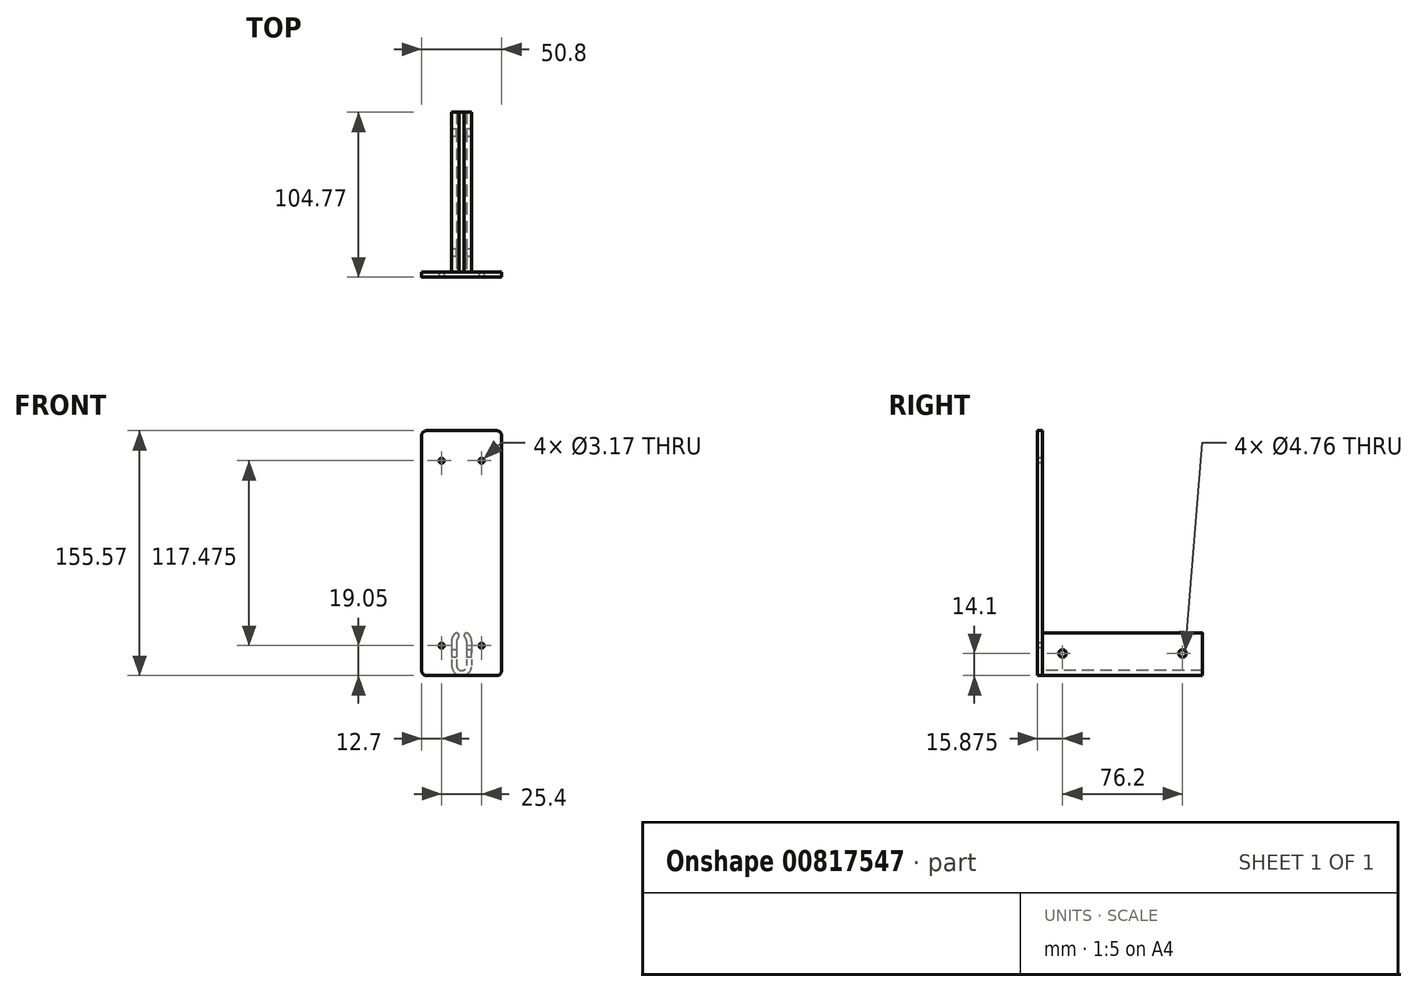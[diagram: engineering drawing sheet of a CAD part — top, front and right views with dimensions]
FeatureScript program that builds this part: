
annotation { "Feature Type Name" : "Feature", "Feature Type Description" : "" }
export const myFeature = defineFeature(function(context is Context, id is Id, definition is map)
    precondition{}
    {
        {
            var Q0;
            Q0=qCreatedBy(makeId("Front.planeOp"),FACE);
            var sketch = newSketch(context, id + "F0", { "sketchPlane" : qUnion([Q0])});
            skLineSegment(sketch, "E0.bottom", {"start": v(-3.18, 0) * mm, "end": v(-47.63, 0) * mm});
            skLineSegment(sketch, "E0.top", {"start": v(-3.18, 155.58) * mm, "end": v(-47.63, 155.58) * mm});
            skLineSegment(sketch, "E0.left", {"start": v(0, 3.17) * mm, "end": v(0, 152.4) * mm});
            skLineSegment(sketch, "E0.right", {"start": v(-50.8, 3.17) * mm, "end": v(-50.8, 152.4) * mm});
            skCircle(sketch, "E1", {"center": v(-38.1, 136.53) * mm, "radius": 1.59 * mm});
            skCircle(sketch, "E2", {"center": v(-12.7, 136.53) * mm, "radius": 1.59 * mm});
            skCircle(sketch, "E3", {"center": v(-12.7, 19.05) * mm, "radius": 1.59 * mm});
            skCircle(sketch, "E4", {"center": v(-38.1, 19.05) * mm, "radius": 1.59 * mm});
            skPoint(sketch, "E5.visualSharp", {"position": v(-50.8, 155.58) * mm});
            skArc(sketch, "E5.filletArc", {"start": v(-47.63, 155.58) * mm, "mid": v(-49.87, 154.65) * mm, "end": v(-50.8, 152.4) * mm});
            skPoint(sketch, "E6.visualSharp", {"position": v(0, 155.58) * mm});
            skArc(sketch, "E6.filletArc", {"start": v(0, 152.4) * mm, "mid": v(-0.93, 154.65) * mm, "end": v(-3.18, 155.58) * mm});
            skPoint(sketch, "E7.visualSharp", {"position": v(0, 0) * mm});
            skArc(sketch, "E7.filletArc", {"start": v(-3.18, 0) * mm, "mid": v(-0.93, 0.93) * mm, "end": v(0, 3.17) * mm});
            skPoint(sketch, "E8.visualSharp", {"position": v(-50.8, 0) * mm});
            skArc(sketch, "E8.filletArc", {"start": v(-50.8, 3.17) * mm, "mid": v(-49.87, 0.93) * mm, "end": v(-47.63, 0) * mm});
            skSolve(sketch);
        }
        {
            var Q0;
            Q0 = qSketchRegion(id + "F0", true);
            extrude(context, id + "F1", {"entities" : qUnion([Q0]), "oppositeDirection" : true, "depth" : 3.17 * mm, "offsetDistance" : 25.4 * mm});
        }
        {
            var Q0;
            Q0=makeQuery(id+"F1.opExtrude","CAP_FACE",FACE,{"disambiguationData":[OSD([sQuery(id+"F0.wireOp",EDGE,"E0.bottom"),sQuery(id+"F0.wireOp",EDGE,"E0.top"),sQuery(id+"F0.wireOp",EDGE,"E0.left"),sQuery(id+"F0.wireOp",EDGE,"E0.right"),sQuery(id+"F0.wireOp",EDGE,"E1"),sQuery(id+"F0.wireOp",EDGE,"E2"),sQuery(id+"F0.wireOp",EDGE,"E3"),sQuery(id+"F0.wireOp",EDGE,"E4"),sQuery(id+"F0.wireOp",EDGE,"E5.filletArc"),sQuery(id+"F0.wireOp",EDGE,"E6.filletArc"),sQuery(id+"F0.wireOp",EDGE,"E7.filletArc"),sQuery(id+"F0.wireOp",EDGE,"E8.filletArc")])],"isStart":false});
            var sketch = newSketch(context, id + "F2", { "sketchPlane" : qUnion([Q0])});
            skLineSegment(sketch, "E9", {"start": v(25.4, 21.85) * mm, "end": v(25.4, 21.85) * mm, "construction": true});
            skLineSegment(sketch, "E10.0", {"start": v(28.58, 21.85) * mm, "end": v(28.58, 6.35) * mm});
            skLineSegment(sketch, "E11.0", {"start": v(22.23, 21.85) * mm, "end": v(22.23, 6.35) * mm});
            skArc(sketch, "E12", {"start": v(22.23, 6.35) * mm, "mid": v(25.4, 3.18) * mm, "end": v(28.58, 6.35) * mm});
            skPoint(sketch, "E13.orphan", {"position": v(25.4, 155.58) * mm});
            skArc(sketch, "E14", {"start": v(26.99, 25.4) * mm, "mid": v(27.13, 24.75) * mm, "end": v(27.52, 24.22) * mm});
            skArc(sketch, "E15", {"start": v(23.28, 24.22) * mm, "mid": v(23.67, 24.75) * mm, "end": v(23.81, 25.4) * mm});
            skPoint(sketch, "E16.visualSharp", {"position": v(28.58, 23.81) * mm});
            skArc(sketch, "E16.filletArc", {"start": v(28.58, 21.85) * mm, "mid": v(28.3, 23.15) * mm, "end": v(27.52, 24.22) * mm});
            skPoint(sketch, "E17.visualSharp", {"position": v(22.23, 23.81) * mm});
            skArc(sketch, "E17.filletArc", {"start": v(23.28, 24.22) * mm, "mid": v(22.5, 23.15) * mm, "end": v(22.23, 21.85) * mm});
            skPoint(sketch, "E18.trimOffspring.end.orphan", {"position": v(25.4, 0) * mm});
            skArc(sketch, "E19.0", {"start": v(31.75, 21.85) * mm, "mid": v(31.2, 24.44) * mm, "end": v(29.63, 26.58) * mm});
            skArc(sketch, "E19.1", {"start": v(21.17, 26.58) * mm, "mid": v(19.6, 24.44) * mm, "end": v(19.05, 21.85) * mm});
            skLineSegment(sketch, "E19.2", {"start": v(19.05, 21.85) * mm, "end": v(19.05, 6.35) * mm});
            skArc(sketch, "E19.3", {"start": v(19.05, 6.35) * mm, "mid": v(25.4, 0) * mm, "end": v(31.75, 6.35) * mm});
            skLineSegment(sketch, "E19.4", {"start": v(31.75, 21.85) * mm, "end": v(31.75, 6.35) * mm});
            skArc(sketch, "E20", {"start": v(29.63, 26.58) * mm, "mid": v(27.93, 26.85) * mm, "end": v(26.99, 25.4) * mm});
            skArc(sketch, "E21", {"start": v(23.81, 25.4) * mm, "mid": v(22.87, 26.85) * mm, "end": v(21.17, 26.58) * mm});
            skSolve(sketch);
        }
        {
            var Q0;
            Q0 = qSketchRegion(id + "F2", true);
            extrude(context, id + "F3", {"entities" : qUnion([Q0]), "operationType" : NewBodyOperationType.ADD, "depth" : 101.6 * mm, "offsetDistance" : 25.4 * mm});
        }
        {
            var Q0;
            Q0=makeQuery(id+"F3.opExtrude","SWEPT_FACE",FACE,{"disambiguationData":[OSD([sQuery(id+"F2.wireOp",EDGE,"E19.2")])]});
            var sketch = newSketch(context, id + "F4", { "sketchPlane" : qUnion([Q0])});
            skLineSegment(sketch, "E22", {"start": v(15.88, 21.85) * mm, "end": v(15.88, 6.35) * mm, "construction": true});
            skLineSegment(sketch, "E23", {"start": v(92.08, 21.85) * mm, "end": v(92.08, 6.35) * mm, "construction": true});
            skCircle(sketch, "E24", {"center": v(15.88, 14.1) * mm, "radius": 2.38 * mm});
            skCircle(sketch, "E25", {"center": v(92.08, 14.1) * mm, "radius": 2.38 * mm});
            skSolve(sketch);
        }
        {
            var Q0;
            Q0 = qSketchRegion(id + "F4", true);
            extrude(context, id + "F5", {"entities" : qUnion([Q0]), "operationType" : NewBodyOperationType.REMOVE, "endBound" : BoundingType.THROUGH_ALL, "oppositeDirection" : true, "depth" : 25.4 * mm, "offsetDistance" : 25.4 * mm});
        }
    });
